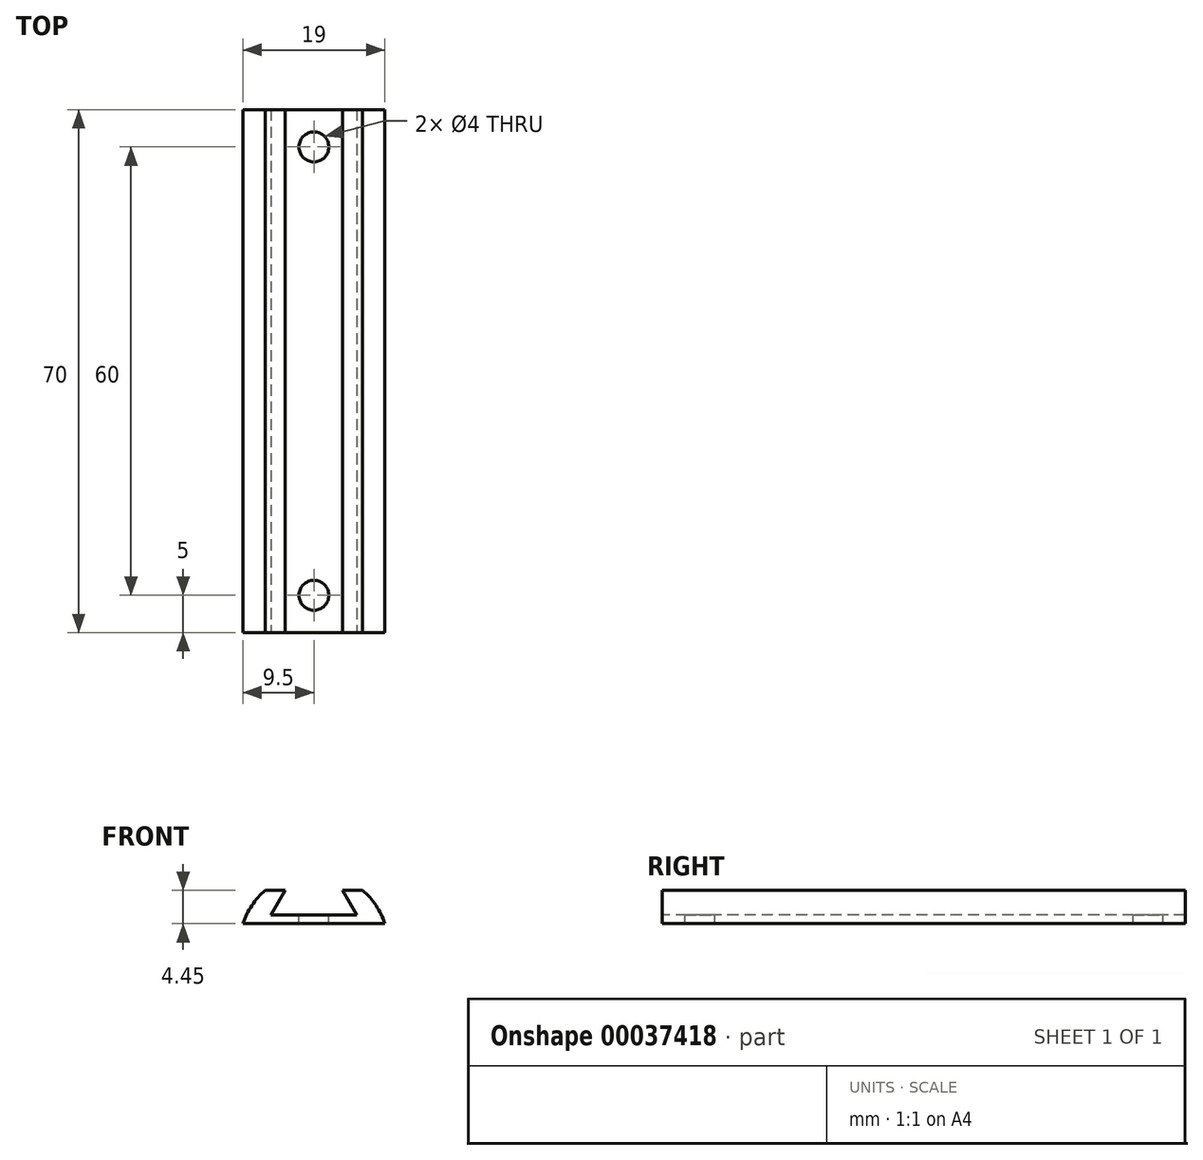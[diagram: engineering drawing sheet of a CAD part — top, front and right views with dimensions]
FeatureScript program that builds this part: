
annotation { "Feature Type Name" : "Feature", "Feature Type Description" : "" }
export const myFeature = defineFeature(function(context is Context, id is Id, definition is map)
    precondition{}
    {
        {
            var Q0;
            Q0=qCreatedBy(makeId("Front.planeOp"),FACE);
            var sketch = newSketch(context, id + "F0", { "sketchPlane" : qUnion([Q0])});
            skArc(sketch, "E0", {"start": v(9.5, 3.12) * mm, "mid": v(8.32, 5.55) * mm, "end": v(6.53, 7.57) * mm});
            skLineSegment(sketch, "E1", {"start": v(-9.5, 3.12) * mm, "end": v(9.5, 3.12) * mm});
            skLineSegment(sketch, "E2", {"start": v(0, 4.27) * mm, "end": v(-5.74, 4.27) * mm});
            skLineSegment(sketch, "E3", {"start": v(-5.74, 4.27) * mm, "end": v(-3.83, 7.57) * mm});
            skLineSegment(sketch, "E4", {"start": v(-3.83, 7.57) * mm, "end": v(-6.53, 7.57) * mm});
            skLineSegment(sketch, "E5.MirrorCS", {"start": v(3.83, 7.57) * mm, "end": v(6.53, 7.57) * mm});
            skLineSegment(sketch, "E6.MirrorCS", {"start": v(0, 4.27) * mm, "end": v(5.74, 4.27) * mm});
            skLineSegment(sketch, "E7.MirrorCS", {"start": v(5.74, 4.27) * mm, "end": v(3.83, 7.57) * mm});
            skArc(sketch, "E8.trimOffspring", {"start": v(-6.53, 7.57) * mm, "mid": v(-8.32, 5.55) * mm, "end": v(-9.5, 3.12) * mm});
            skPoint(sketch, "E9.end.orphan", {"position": v(-2.33, 7.57) * mm});
            skPoint(sketch, "E10.end.orphan", {"position": v(-3.63, 5.32) * mm});
            skSolve(sketch);
        }
        {
            var Q0;
            Q0=makeQuery(id+"F0.imprint","IMPRINT",FACE,{"disambiguationData":[TD([[makeQuery(id+"F0.imprint","IMPRINT",EDGE,{"derivedFrom":sQuery(id+"F0.wireOp",EDGE,"E0")}),1.0]])]});
            extrude(context, id + "F1", {"entities" : qUnion([Q0]), "oppositeDirection" : true, "depth" : 70 * mm});
        }
        {
            var Q0;
            Q0=makeQuery(id+"F1.opExtrude","SWEPT_FACE",FACE,{"disambiguationData":[OSD([sQuery(id+"F0.wireOp",EDGE,"E2"),sQuery(id+"F0.wireOp",EDGE,"E6.MirrorCS")])]});
            var sketch = newSketch(context, id + "F2", { "sketchPlane" : qUnion([Q0])});
            skCircle(sketch, "E11", {"center": v(0, 5) * mm, "radius": 2 * mm});
            skPoint(sketch, "E11.centerSnap0", {"position": v(0, 0) * mm});
            skLineSegment(sketch, "E12", {"start": v(-13.75, 35) * mm, "end": v(17.02, 35) * mm});
            skCircle(sketch, "E13.MirrorC", {"center": v(0, 65) * mm, "radius": 2 * mm});
            skSolve(sketch);
        }
        {
            var Q0;
            Q0 = qSketchRegion(id + "F2", true);
            extrude(context, id + "F3", {"entities" : qUnion([Q0]), "operationType" : NewBodyOperationType.REMOVE, "endBound" : BoundingType.THROUGH_ALL, "oppositeDirection" : true, "depth" : 25 * mm});
        }
    });
